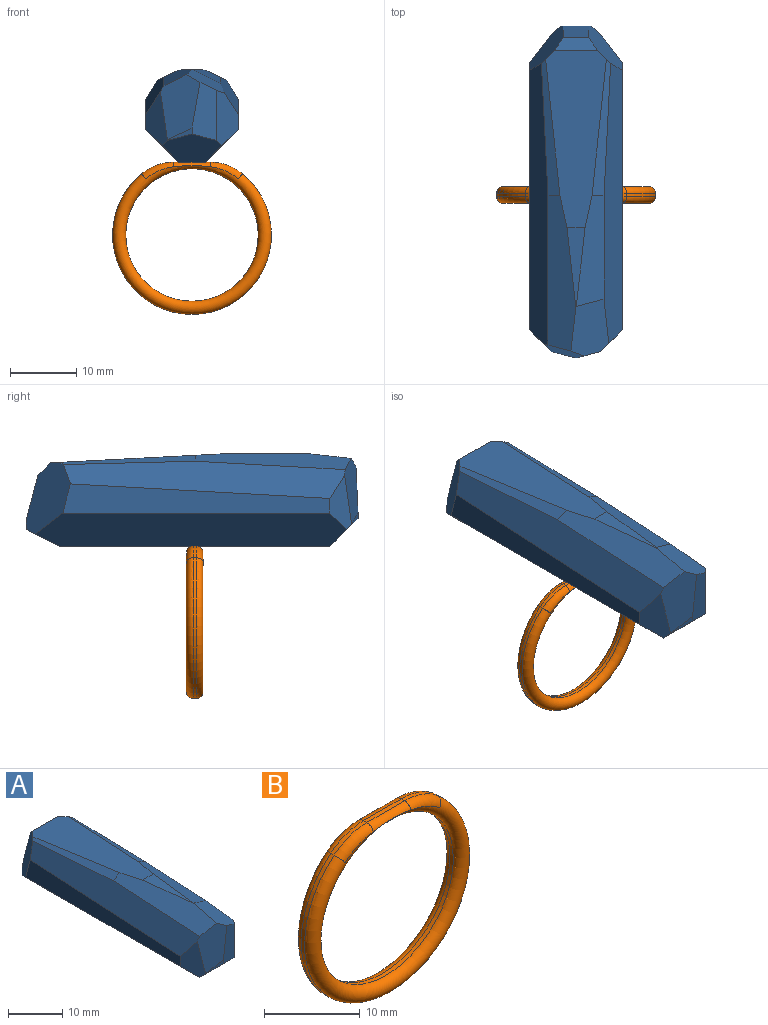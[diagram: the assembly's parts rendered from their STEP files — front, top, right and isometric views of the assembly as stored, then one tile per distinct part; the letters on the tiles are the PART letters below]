
ASSEMBLY  parts=2 mates=1
PART A: 26 faces, bbox 14x50.2x14 mm
  f0: plane 40.84x4mm, normal (0,0,-1), area 163.4mm2, adj f8,f12,f13,f16
  f1: plane 40.37x4.42mm, normal (1,0,0), area 132.9mm2, adj f6,f11,f12,f14
  f2: plane 12.11x2.75mm, normal (0,0,1), area 16.9mm2, adj f5,f20,f23,f25
  f3: plane 4.5x1.3mm, normal (0,1,0), area 5.4mm2, adj f9,f13,f14,f15
  f4: plane 20.54x2.8mm, normal (0.45,0,0.89), area 28.2mm2, adj f5,f11,f14,f23
  f5: plane 16.79x4.19mm, normal (0.45,-0.05,0.89), area 57.2mm2, adj f2,f4,f11,f23,f25
  f6: plane 8.37x3.28mm, normal (0.71,-0.71,0), area 27.7mm2, adj f1,f8,f10,f11,f12,f25
  f7: plane 6.53x1.88mm, normal (0,0.71,0.71), area 13.8mm2, adj f9,f14,f15,f23
  f8: plane 9x4.25mm, normal (0,-0.71,-0.71), area 37.2mm2, adj f0,f6,f10,f12,f16,f18,f19
  f9: plane 6.88x3.84mm, normal (0,0.97,0.25), area 27.3mm2, adj f3,f7,f14,f15
  f10: plane 8.8x3.72mm, normal (0.25,-0.97,0), area 26.1mm2, adj f6,f8,f18,f24,f25
  f11: plane 42.33x5.62mm, normal (0.85,-0.03,0.53), area 193.7mm2, adj f1,f4,f5,f6,f14,f25
  f12: plane 46.98x5mm, normal (0.71,0,-0.71), area 309.4mm2, adj f0,f1,f6,f8,f13,f14
  f13: plane 7.64x5.08mm, normal (0,0.45,-0.89), area 33.5mm2, adj f0,f3,f12,f14,f15,f16
  f14: plane 10.85x6.71mm, normal (0.71,0.68,0.18), area 64.8mm2, adj f1,f3,f4,f7,f9,f11,f12,f13
  f15: plane 10.85x6.71mm, normal (-0.71,0.68,0.18), area 64.8mm2, adj f3,f7,f9,f13,f16,f17,f21,f22
  f16: plane 46.98x5mm, normal (-0.71,0,-0.71), area 309.4mm2, adj f0,f8,f13,f15,f19,f22
  f17: plane 42.58x5.62mm, normal (-0.85,-0.03,0.53), area 198.5mm2, adj f15,f19,f20,f21,f22,f24
  f18: plane 3.72x1.88mm, normal (-0.25,-0.97,0), area 1.9mm2, adj f8,f10,f19,f24
  f19: plane 8.21x3.28mm, normal (-0.71,-0.71,0), area 22.3mm2, adj f8,f16,f17,f18,f22,f24
  f20: plane 23.53x4.21mm, normal (-0.45,-0.05,0.89), area 87mm2, adj f2,f17,f21,f23,f24,f25
  f21: plane 20.54x2.8mm, normal (-0.45,0,0.89), area 28.2mm2, adj f15,f17,f20,f23
  f22: plane 40.37x4.42mm, normal (-1,0,0), area 132.9mm2, adj f15,f16,f17,f19
  f23: plane 26.8x9.17mm, normal (0,0.05,1), area 173.8mm2, adj f2,f4,f5,f7,f14,f15,f20,f21
  f24: plane 9.9x5.98mm, normal (-0.29,-0.95,0.09), area 42.5mm2, adj f10,f17,f18,f19,f20,f25
  f25: plane 8.56x5.72mm, normal (0.46,-0.15,0.87), area 43.2mm2, adj f2,f5,f6,f10,f11,f20,f24
PART B: 13 faces, bbox 26x2.5x26 mm
  f0: plane 5.57x0.5mm, normal (0,0,1), area 2.8mm2, adj f3,f4,f8,f12
  f1: cylinder r=10mm len=20mm, axis (0,1,0), area 31.4mm2, adj f5,f9
  f2: cylinder r=12mm len=24mm, axis (0,1,0), area 29.4mm2, adj f3,f4,f5,f9
  f3: cylinder r=7.62mm len=4.85mm, axis (0,1,0), area 2.6mm2, adj f0,f2,f7,f10
  f4: cylinder r=7.62mm len=4.85mm, axis (0,1,0), area 2.6mm2, adj f0,f2,f6,f11
  f5: torus R=11mm, axis (0,-1,0), area 187.9mm2, adj f1,f2,f6,f7,f8
  f6: torus R=6.62mm, axis (0,-1,0), area 7.1mm2, adj f4,f5,f8
  f7: torus R=6.62mm, axis (0,-1,0), area 7.1mm2, adj f3,f5,f8
  f8: cylinder r=1mm len=5.57mm, axis (1,0,0), area 6.2mm2, adj f0,f5,f6,f7
  f9: torus R=11mm, axis (0,-1,0), area 187.9mm2, adj f1,f2,f10,f11,f12
  f10: torus R=6.62mm, axis (0,-1,0), area 7.1mm2, adj f3,f9,f12
  f11: torus R=6.62mm, axis (0,-1,0), area 7.1mm2, adj f4,f9,f12
  f12: cylinder r=1mm len=5.57mm, axis (-1,0,0), area 6.2mm2, adj f0,f9,f10,f11
PLACE A t=(3.88,0.54,16.7)mm
PLACE B t=(3.88,2.29,-1.3)mm
MATE fastened A.f0 <-> B.f0  axis (0,0,-1) through (3.88,1.04,9.7)mm
